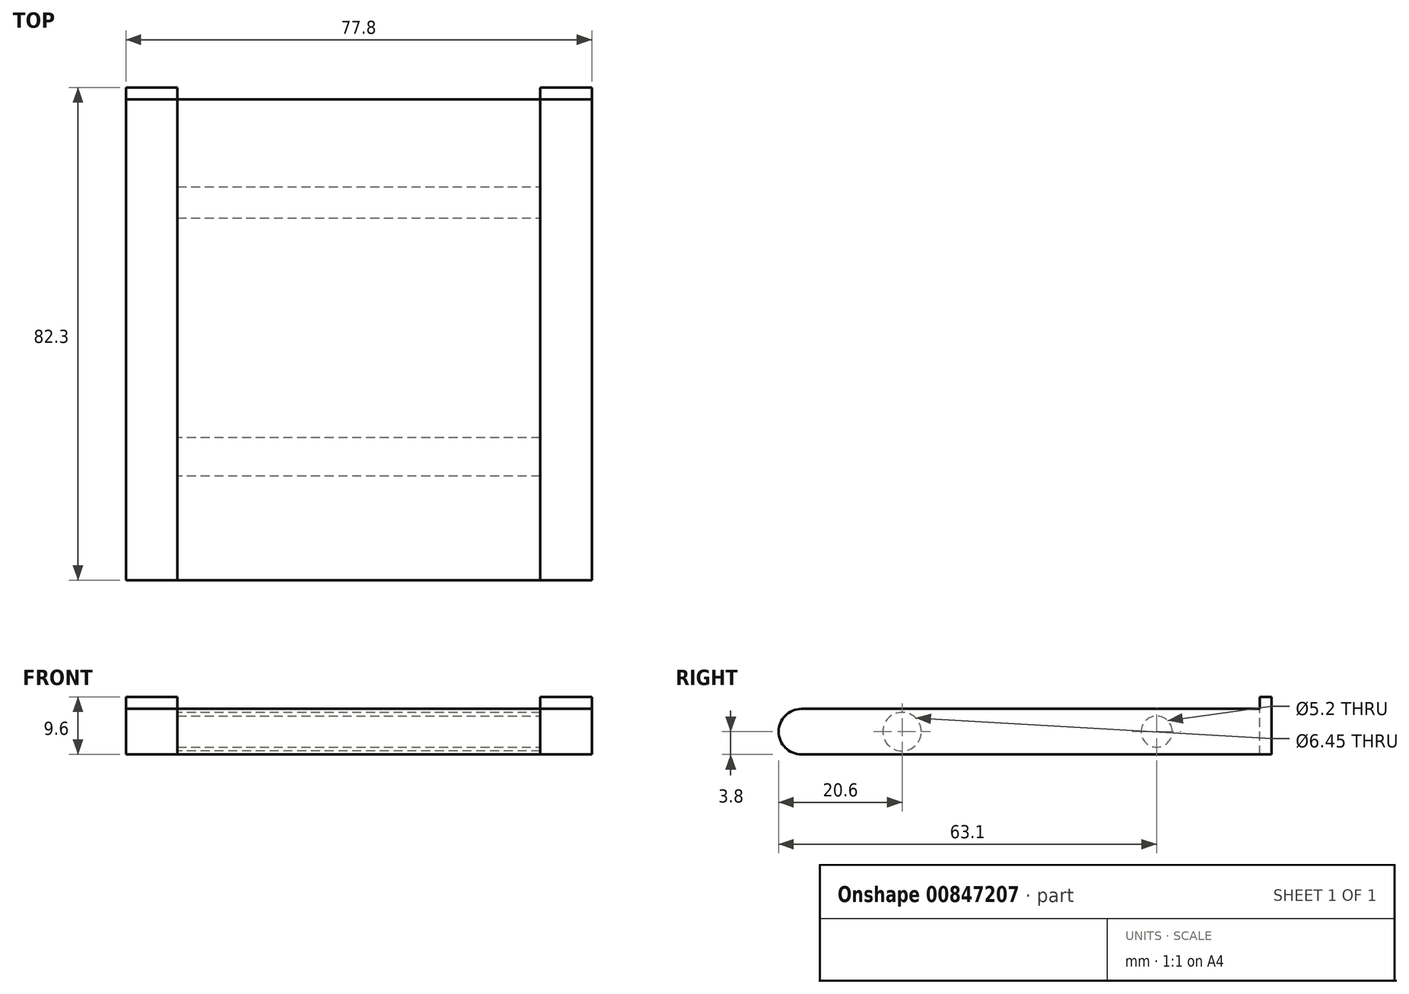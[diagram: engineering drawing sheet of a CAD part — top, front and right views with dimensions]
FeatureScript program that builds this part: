
annotation { "Feature Type Name" : "Feature", "Feature Type Description" : "" }
export const myFeature = defineFeature(function(context is Context, id is Id, definition is map)
    precondition{}
    {
        {
            var Q0;
            Q0=qCreatedBy(makeId("Top.planeOp"),FACE);
            var sketch = newSketch(context, id + "F0", { "sketchPlane" : qUnion([Q0])});
            skLineSegment(sketch, "E0.bottom", {"start": v(-30.3, 39.25) * mm, "end": v(-38.9, 39.25) * mm});
            skLineSegment(sketch, "E0.top", {"start": v(-30.3, -39.25) * mm, "end": v(-38.9, -39.25) * mm});
            skLineSegment(sketch, "E0.left", {"start": v(-30.3, 39.25) * mm, "end": v(-30.3, -39.25) * mm});
            skLineSegment(sketch, "E0.right", {"start": v(-38.9, 39.25) * mm, "end": v(-38.9, -39.25) * mm});
            skPoint(sketch, "E0.middle", {"position": v(-34.6, 0) * mm});
            skLineSegment(sketch, "E1", {"start": v(-69.2, 39.25) * mm, "end": v(0, 39.25) * mm, "construction": true});
            skSolve(sketch);
        }
        {
            var Q0;
            Q0=makeQuery(id+"F0.imprint","IMPRINT",FACE,{"disambiguationData":[TD([[makeQuery(id+"F0.imprint","IMPRINT",EDGE,{"derivedFrom":sQuery(id+"F0.wireOp",EDGE,"E0.bottom")}),1.0]])]});
            var Q1;
            Q1=makeQuery(id+"F0.imprint","IMPRINT",FACE,{"disambiguationData":[TD([[makeQuery(id+"F0.imprint","IMPRINT",EDGE,{"derivedFrom":sQuery(id+"F0.wireOp",EDGE,"7c6f704d-18fb-40f0-8486-a0e4ee1fdf740.MirrorCS")}),1.0]])]});
            extrude(context, id + "F1", {"entities" : qUnion([Q0, Q1]), "depth" : 7.6 * mm, "offsetDistance" : 25 * mm});
        }
        {
            var Q0;
            Q0=makeQuery(id+"F1.opExtrude","SWEPT_FACE",FACE,{"disambiguationData":[OSD([sQuery(id+"F0.wireOp",EDGE,"E0.right")])]});
            var sketch = newSketch(context, id + "F2", { "sketchPlane" : qUnion([Q0])});
            skArc(sketch, "E2", {"start": v(39.25, 0) * mm, "mid": v(43.05, 3.8) * mm, "end": v(39.25, 7.6) * mm});
            skSolve(sketch);
        }
        {
            var Q0;
            Q0=makeQuery(id+"F2.imprint","IMPRINT",FACE,{"disambiguationData":[TD([[makeQuery(id+"F2.imprint","IMPRINT",EDGE,{"derivedFrom":sQuery(id+"F2.wireOp",EDGE,"E2")}),1.0]])]});
            extrude(context, id + "F3", {"entities" : qUnion([Q0]), "operationType" : NewBodyOperationType.ADD, "oppositeDirection" : true, "depth" : 8.6 * mm, "offsetDistance" : 25 * mm});
        }
        {
            var Q0;
            Q0=makeQuery(id+"F1.opExtrude","CAP_FACE",FACE,{"disambiguationData":[OSD([sQuery(id+"F0.wireOp",EDGE,"E0.bottom"),sQuery(id+"F0.wireOp",EDGE,"E0.top"),sQuery(id+"F0.wireOp",EDGE,"E0.left"),sQuery(id+"F0.wireOp",EDGE,"E0.right")])],"isStart":false});
            var sketch = newSketch(context, id + "F4", { "sketchPlane" : qUnion([Q0])});
            skLineSegment(sketch, "E3.bottom", {"start": v(-38.9, 39.25) * mm, "end": v(-30.3, 39.25) * mm});
            skLineSegment(sketch, "E3.top", {"start": v(-38.9, 37.25) * mm, "end": v(-30.3, 37.25) * mm});
            skLineSegment(sketch, "E3.left", {"start": v(-38.9, 39.25) * mm, "end": v(-38.9, 37.25) * mm});
            skLineSegment(sketch, "E3.right", {"start": v(-30.3, 39.25) * mm, "end": v(-30.3, 37.25) * mm});
            skSolve(sketch);
        }
        {
            var Q0;
            Q0 = qSketchRegion(id + "F4", true);
            extrude(context, id + "F5", {"entities" : qUnion([Q0]), "operationType" : NewBodyOperationType.ADD, "depth" : 2 * mm, "offsetDistance" : 25 * mm});
        }
        {
            var Q0;
            Q0=makeQuery(id+"F3.boolean.opBoolean","MERGE",FACE,{"derivedFrom":[makeQuery(id+"F1.opExtrude","SWEPT_FACE",FACE,{"disambiguationData":[OSD([sQuery(id+"F0.wireOp",EDGE,"E0.left")])]}),makeQuery(id+"F3.opExtrude","CAP_FACE",FACE,{"disambiguationData":[OSD([sQuery(id+"F0.wireOp",EDGE,"E0.top"),sQuery(id+"F0.wireOp",EDGE,"E0.right"),sQuery(id+"F2.wireOp",EDGE,"E2")])],"isStart":false})]});
            var sketch = newSketch(context, id + "F6", { "sketchPlane" : qUnion([Q0])});
            skCircle(sketch, "E4", {"center": v(-22.45, 3.8) * mm, "radius": 3.23 * mm});
            skLineSegment(sketch, "E5", {"start": v(-22.45, 0) * mm, "end": v(-22.45, 7.6) * mm, "construction": true});
            skSolve(sketch);
        }
        {
            var Q0;
            Q0=makeQuery(id+"F6.imprint","IMPRINT",FACE,{"disambiguationData":[TD([[makeQuery(id+"F6.imprint","IMPRINT",EDGE,{"derivedFrom":sQuery(id+"F6.wireOp",EDGE,"E4")}),1.0]])]});
            extrude(context, id + "F7", {"entities" : qUnion([Q0]), "operationType" : NewBodyOperationType.ADD, "depth" : 30.3 * mm, "offsetDistance" : 25 * mm});
        }
        {
            var Q0;
            Q0=makeQuery(id+"F1.opExtrude","SWEPT_BODY",BODY,{"disambiguationData":[OSD([sQuery(id+"F0.wireOp",EDGE,"E0.bottom"),sQuery(id+"F0.wireOp",EDGE,"E0.top"),sQuery(id+"F0.wireOp",EDGE,"E0.left"),sQuery(id+"F0.wireOp",EDGE,"E0.right")])]});
            var Q1;
            Q1=qCreatedBy(makeId("Right.planeOp"),FACE);
            mirror(context, id + "F8", {"operationType" : NewBodyOperationType.ADD, "entities" : qUnion([Q0]), "mirrorPlane" : qUnion([Q1])});
        }
        {
            var Q0;
            Q0=makeQuery(id+"F8.opPattern","COPY",FACE,{"derivedFrom":makeQuery(id+"F1.opExtrude","CAP_FACE",FACE,{"disambiguationData":[OSD([sQuery(id+"F0.wireOp",EDGE,"E0.bottom"),sQuery(id+"F0.wireOp",EDGE,"E0.top"),sQuery(id+"F0.wireOp",EDGE,"E0.left"),sQuery(id+"F0.wireOp",EDGE,"E0.right")])],"isStart":false}),"instanceName":"1"});
            var sketch = newSketch(context, id + "F9", { "sketchPlane" : qUnion([Q0])});
            skLineSegment(sketch, "E6.bottom", {"start": v(30.3, 37.25) * mm, "end": v(-30.3, 37.25) * mm});
            skLineSegment(sketch, "E6.top", {"start": v(30.3, -39.25) * mm, "end": v(-30.3, -39.25) * mm});
            skLineSegment(sketch, "E6.left", {"start": v(30.3, 37.25) * mm, "end": v(30.3, -39.25) * mm});
            skLineSegment(sketch, "E6.right", {"start": v(-30.3, 37.25) * mm, "end": v(-30.3, -39.25) * mm});
            skSolve(sketch);
        }
        {
            var Q0;
            Q0 = qSketchRegion(id + "F9", true);
            extrude(context, id + "F10", {"entities" : qUnion([Q0]), "oppositeDirection" : true, "depth" : 7.6 * mm, "offsetDistance" : 25 * mm});
        }
        {
            var Q0;
            Q0=makeQuery(id+"F10.opExtrude","SWEPT_FACE",FACE,{"disambiguationData":[OSD([sQuery(id+"F9.wireOp",EDGE,"E6.right")])]});
            var sketch = newSketch(context, id + "F11", { "sketchPlane" : qUnion([Q0])});
            skArc(sketch, "E7", {"start": v(39.25, 0) * mm, "mid": v(43.05, 3.8) * mm, "end": v(39.25, 7.6) * mm});
            skSolve(sketch);
        }
        {
            var Q0;
            Q0=makeQuery(id+"F11.imprint","IMPRINT",FACE,{"disambiguationData":[TD([[makeQuery(id+"F11.imprint","IMPRINT",EDGE,{"derivedFrom":sQuery(id+"F11.wireOp",EDGE,"E7")}),1.0]])]});
            extrude(context, id + "F12", {"entities" : qUnion([Q0]), "oppositeDirection" : true, "depth" : 60.6 * mm, "offsetDistance" : 25 * mm});
        }
        {
            var Q0;
            Q0=makeQuery(id+"F12.opExtrude","SWEPT_BODY",BODY,{"disambiguationData":[OSD([sQuery(id+"F9.wireOp",EDGE,"E6.top"),sQuery(id+"F9.wireOp",EDGE,"E6.right"),sQuery(id+"F11.wireOp",EDGE,"E7")])]});
            var Q1;
            Q1=makeQuery(id+"F10.opExtrude","SWEPT_BODY",BODY,{"disambiguationData":[OSD([sQuery(id+"F9.wireOp",EDGE,"E6.bottom"),sQuery(id+"F9.wireOp",EDGE,"E6.top"),sQuery(id+"F9.wireOp",EDGE,"E6.left"),sQuery(id+"F9.wireOp",EDGE,"E6.right")])]});
            booleanBodies(context, id + "F13", {"operationType" : BooleanOperationType.UNION, "tools" : qUnion([Q0, Q1])});
        }
        {
            var Q0;
            Q0=makeQuery(id+"F13.opBoolean","MERGE",FACE,{"derivedFrom":[makeQuery(id+"F10.opExtrude","SWEPT_FACE",FACE,{"disambiguationData":[OSD([sQuery(id+"F9.wireOp",EDGE,"E6.left")])]}),makeQuery(id+"F12.opExtrude","CAP_FACE",FACE,{"disambiguationData":[OSD([sQuery(id+"F9.wireOp",EDGE,"E6.top"),sQuery(id+"F9.wireOp",EDGE,"E6.right"),sQuery(id+"F11.wireOp",EDGE,"E7")])],"isStart":false})]});
            var sketch = newSketch(context, id + "F14", { "sketchPlane" : qUnion([Q0])});
            skCircle(sketch, "E8", {"center": v(20.05, 3.8) * mm, "radius": 2.6 * mm});
            skPoint(sketch, "E8.centerSnap0", {"position": v(37.25, 3.8) * mm});
            skSolve(sketch);
        }
        {
            var Q0;
            Q0=makeQuery(id+"F14.imprint","IMPRINT",FACE,{"disambiguationData":[TD([[makeQuery(id+"F14.imprint","IMPRINT",EDGE,{"derivedFrom":sQuery(id+"F14.wireOp",EDGE,"E8")}),1.0]])]});
            extrude(context, id + "F15", {"entities" : qUnion([Q0]), "operationType" : NewBodyOperationType.REMOVE, "oppositeDirection" : true, "depth" : 60.6 * mm, "offsetDistance" : 25 * mm});
        }
        {
            var Q0;
            Q0=makeQuery(id+"F10.opExtrude","CAP_FACE",FACE,{"disambiguationData":[OSD([sQuery(id+"F9.wireOp",EDGE,"E6.bottom"),sQuery(id+"F9.wireOp",EDGE,"E6.top"),sQuery(id+"F9.wireOp",EDGE,"E6.left"),sQuery(id+"F9.wireOp",EDGE,"E6.right")])],"isStart":false});
            var sketch = newSketch(context, id + "F16", { "sketchPlane" : qUnion([Q0])});
            skSolve(sketch);
        }
        {
            var Q0;
            Q0=makeQuery(id+"F1.opExtrude","SWEPT_BODY",BODY,{"disambiguationData":[OSD([sQuery(id+"F0.wireOp",EDGE,"E0.bottom"),sQuery(id+"F0.wireOp",EDGE,"E0.top"),sQuery(id+"F0.wireOp",EDGE,"E0.left"),sQuery(id+"F0.wireOp",EDGE,"E0.right")])]});
            var Q1;
            Q1=makeQuery(id+"F12.opExtrude","SWEPT_BODY",BODY,{"disambiguationData":[OSD([sQuery(id+"F9.wireOp",EDGE,"E6.top"),sQuery(id+"F9.wireOp",EDGE,"E6.right"),sQuery(id+"F11.wireOp",EDGE,"E7")])]});
            booleanBodies(context, id + "F17", {"operationType" : BooleanOperationType.SUBTRACTION, "tools" : qUnion([Q0]), "targets" : qUnion([Q1]), "keepTools" : true});
        }
    });
